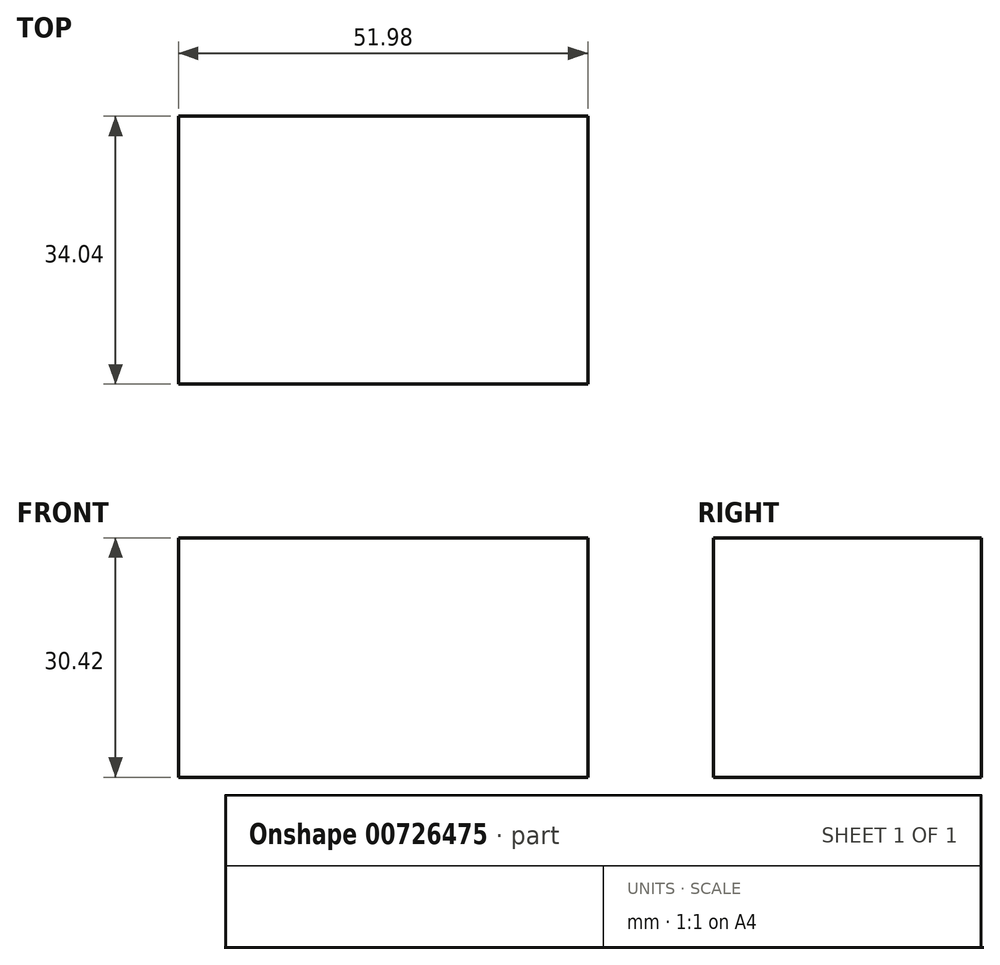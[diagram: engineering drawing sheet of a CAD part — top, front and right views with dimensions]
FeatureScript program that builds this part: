
annotation { "Feature Type Name" : "Feature", "Feature Type Description" : "" }
export const myFeature = defineFeature(function(context is Context, id is Id, definition is map)
    precondition{}
    {
        {
            var Q0;
            Q0=qCreatedBy(makeId("Front.planeOp"),FACE);
            var sketch = newSketch(context, id + "F0", { "sketchPlane" : qUnion([Q0])});
            skLineSegment(sketch, "E0.bottom", {"start": v(-64.06, 44.15) * mm, "end": v(-12.08, 44.15) * mm});
            skLineSegment(sketch, "E0.top", {"start": v(-64.06, 13.73) * mm, "end": v(-12.08, 13.73) * mm});
            skLineSegment(sketch, "E0.left", {"start": v(-64.06, 44.15) * mm, "end": v(-64.06, 13.73) * mm});
            skLineSegment(sketch, "E0.right", {"start": v(-12.08, 44.15) * mm, "end": v(-12.08, 13.73) * mm});
            skSolve(sketch);
        }
        {
            var Q0;
            Q0=makeQuery(id+"F0.imprint","IMPRINT",FACE,{"disambiguationData":[TD([[makeQuery(id+"F0.imprint","IMPRINT",EDGE,{"derivedFrom":sQuery(id+"F0.wireOp",EDGE,"E0.bottom")}),-1.0]])]});
            extrude(context, id + "F1", {"entities" : qUnion([Q0]), "oppositeDirection" : true, "depth" : 34.04 * mm, "offsetDistance" : 25.4 * mm});
        }
    });
